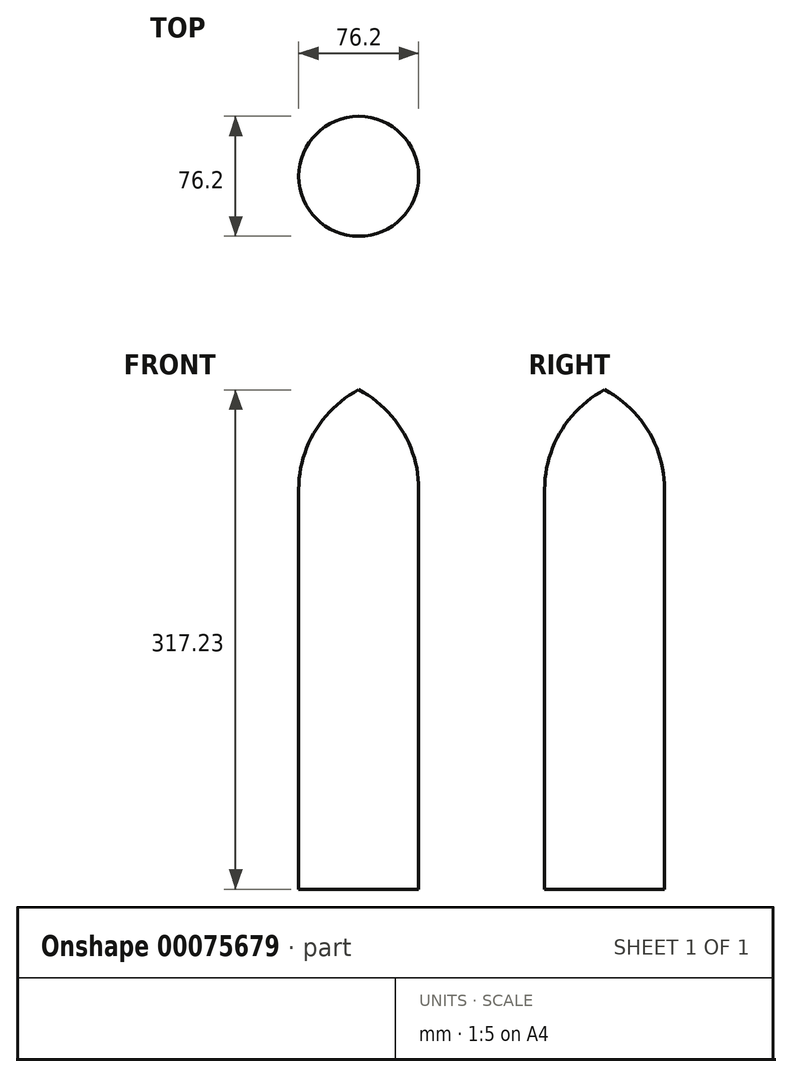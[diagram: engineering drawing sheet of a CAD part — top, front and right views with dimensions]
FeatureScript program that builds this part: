
annotation { "Feature Type Name" : "Feature", "Feature Type Description" : "" }
export const myFeature = defineFeature(function(context is Context, id is Id, definition is map)
    precondition{}
    {
        {
            var Q0;
            Q0=qCreatedBy(makeId("Front.planeOp"),FACE);
            var sketch = newSketch(context, id + "F0", { "sketchPlane" : qUnion([Q0])});
            skLineSegment(sketch, "E0", {"start": v(0, -19.46) * mm, "end": v(38.1, -19.46) * mm});
            skArc(sketch, "E1", {"start": v(38.1, -19.46) * mm, "mid": v(27.84, 17.46) * mm, "end": v(0, 43.77) * mm});
            skLineSegment(sketch, "E2", {"start": v(0, 43.77) * mm, "end": v(0, -19.46) * mm});
            skSolve(sketch);
        }
        {
            var Q0;
            Q0 = qSketchRegion(id + "F0", true);
            var Q1;
            Q1=sQuery(id+"F0.wireOp",EDGE,"E2");
            revolve(context, id + "F1", {"entities" : qUnion([Q0]), "axis" : qUnion([Q1]), "revolveType" : RevolveType.FULL});
        }
        {
            var Q0;
            Q0=makeQuery(id+"F1.opRevolve","SWEPT_FACE",FACE,{"disambiguationData":[OSD([sQuery(id+"F0.wireOp",EDGE,"E0")])]});
            extrude(context, id + "F2", {"entities" : qUnion([Q0]), "operationType" : NewBodyOperationType.ADD, "depth" : 254 * mm});
        }
    });
